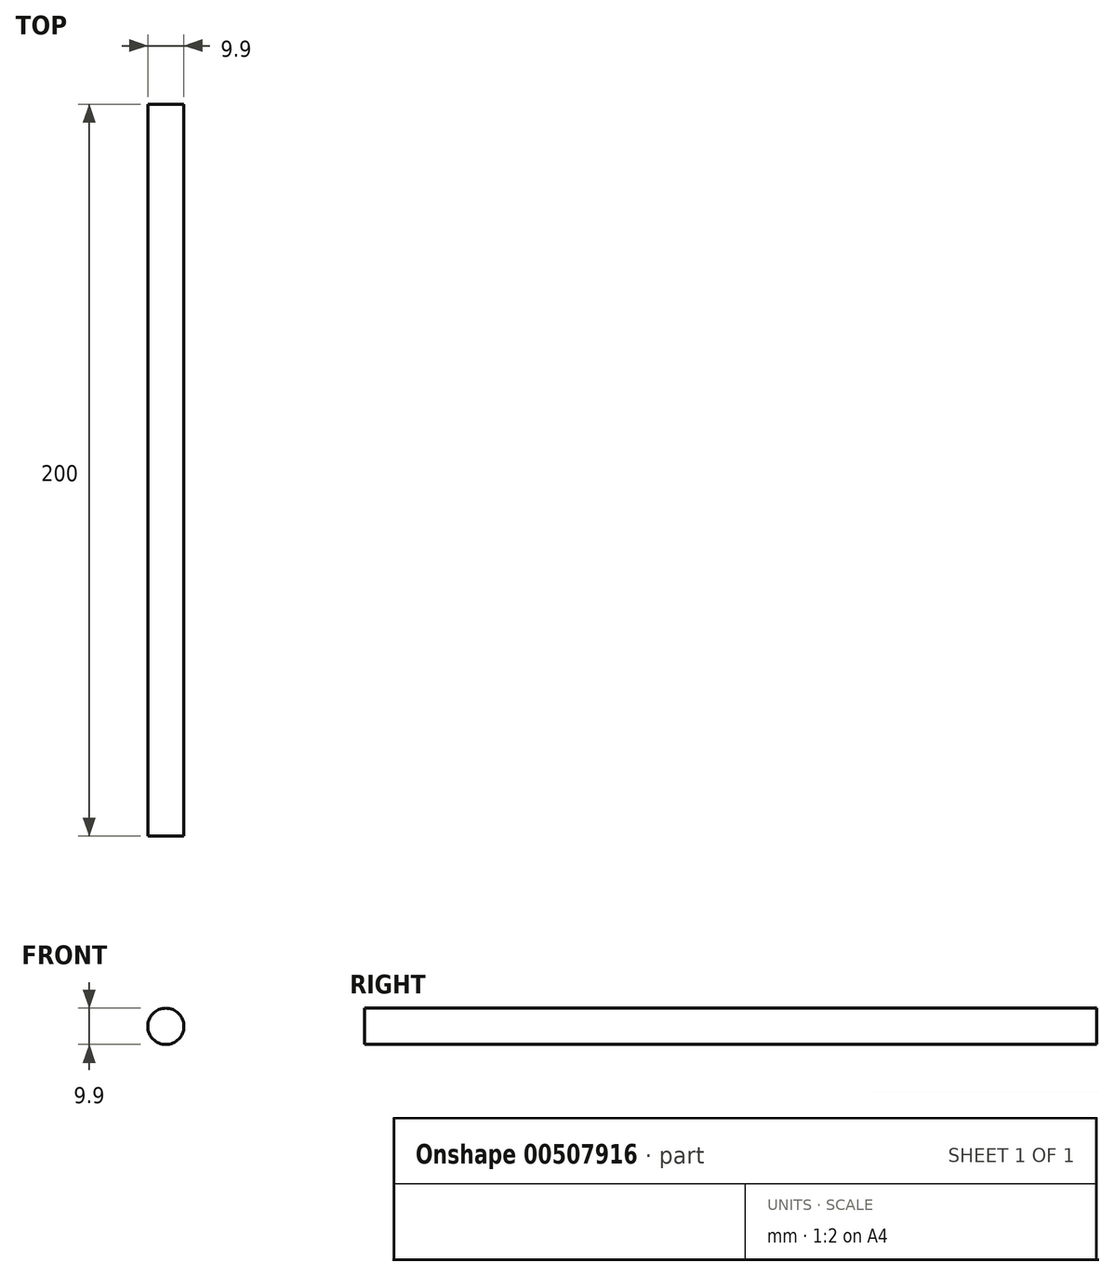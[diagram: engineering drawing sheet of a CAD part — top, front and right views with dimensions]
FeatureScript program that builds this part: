
annotation { "Feature Type Name" : "Feature", "Feature Type Description" : "" }
export const myFeature = defineFeature(function(context is Context, id is Id, definition is map)
    precondition{}
    {
        {
            var Q0;
            Q0=qCreatedBy(makeId("Front.planeOp"),FACE);
            var sketch = newSketch(context, id + "F0", { "sketchPlane" : qUnion([Q0])});
            skCircle(sketch, "E0", {"center": v(0, 0) * mm, "radius": 4.95 * mm});
            skSolve(sketch);
        }
        {
            var Q0;
            Q0=makeQuery(id+"F0.imprint","IMPRINT",FACE,{"disambiguationData":[TD([[makeQuery(id+"F0.imprint","IMPRINT",EDGE,{"derivedFrom":sQuery(id+"F0.wireOp",EDGE,"E0")}),1.0]])]});
            var Q1;
            Q1=sQuery(id+"F0.wireOp",EDGE,"E0");
            extrude(context, id + "F1", {"entities" : qUnion([Q0]), "surfaceEntities" : qUnion([Q1]), "depth" : 200 * mm, "offsetDistance" : 25 * mm});
        }
    });
